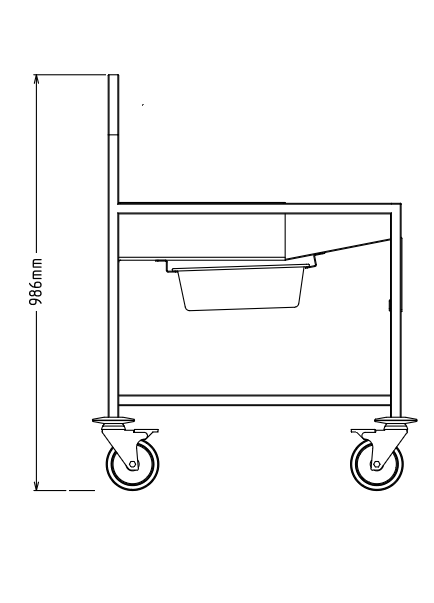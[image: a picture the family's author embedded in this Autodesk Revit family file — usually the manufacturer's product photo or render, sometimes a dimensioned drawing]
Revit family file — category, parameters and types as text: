
# Revit family: QF_ELECTROLUXPROFESSIONAL_650065_TR210TROLLEY
name_source: partatom
category: Attrezzature speciali
units: mm (PartAtom-declared; Revit-internal decimal feet)

## family parameters
Basato su piano di lavoro = No
Condiviso = No
Punto di calcolo locali = No
Quota connettore circolare = Usa diametro
Sempre verticale = Sì
Taglio con vuoti quando caricato = No
Tipo di parte = Normale

## types (1)
- Standard
    Accessory = Sì
    Cold Water Size = 0 mm
    Compressed Air Pressure = 0.0 Pa
    Compressed Air Size = 0 mm
    Compressed Air Volume = 0.0 L/s
    Condensate Return Size = 0 mm
    Cycle = 0 Hz
    Depth Actual = 730 mm  [stored 2.39501 ft]
    Descrizione = SS TROLLEY FOR TR 210 WITH 1/1 GN TRAY RAILS
    Direct Waste Size = 0 mm
    Gas Input Pressure = 0
    Gas KW = 0
    Gas Size = 0 mm
    HP = 0 HP
    Height Actual = 1020 mm  [stored 3.34646 ft]
    Hot Water Size = 0 mm
    Item Number = 650065
    Length Actual = 600 mm
    Modello = TR210trolley
    Phase = 0
    Produttore = Electrolux Professional
    Prospetto di default = 0 mm  [stored 0 ft]
    Refrigerant Compressor Remote = Sì
    Refrigeration Liquid Line Size = 0 mm  [stored 0 ft]
    Refrigeration Suction Line Size = 0 mm  [stored 0 ft]
    Steam Consumption per Hour = 0
    Steam Supply Maximum Pressure = 0.0 Pa
    Steam Supply Minimum Pressure = 0.0 Pa
    Steam Supply Size = 0 mm
    URL = https://www.electroluxprofessional.com
    URL Manufacturer = https://www.electroluxprofessional.com
    Volts = 0 V
    Watts = 0 W
    Weight = 20.70 kg

note: source unit labels omitted for Gas Input Pressure — the stored unit's dimension contradicts the parameter name (converter mislabeling)

note: [stored X ft] marks values corroborated as IEEE doubles in the binary element streams (Revit-internal decimal feet)

## geometry (parser evidence)
native form markers: Sweep x2
no freeform markers — native parametric forms only
